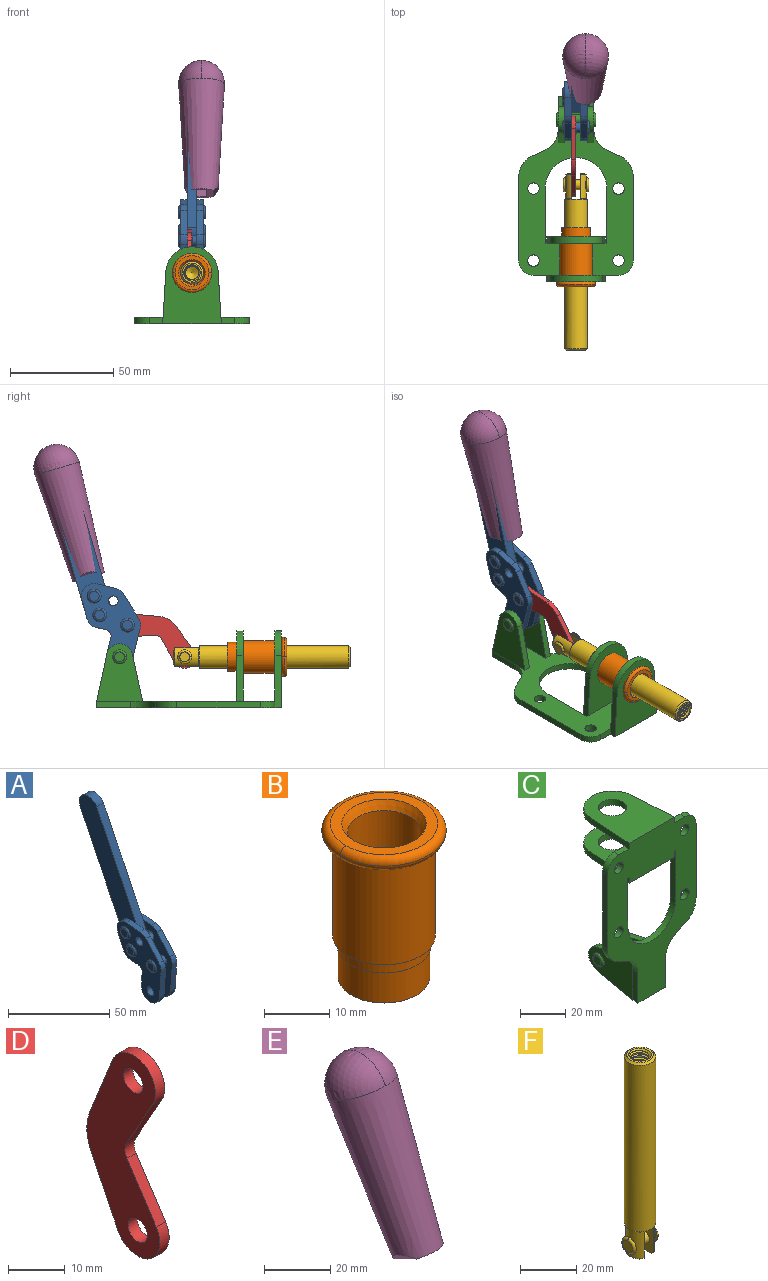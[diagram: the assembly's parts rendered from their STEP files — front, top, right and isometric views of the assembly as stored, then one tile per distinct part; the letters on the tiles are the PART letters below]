
ASSEMBLY  parts=6 mates=6
PART A: 59 faces, bbox 12.9x60.2x99.6 mm
  f0: torus R=2.39mm, axis (-1,0,0), area 14.9mm2, adj f20,f43,f51
  f1: torus R=2.39mm, axis (-1,0,0), area 14.9mm2, adj f19,f42,f51
  f2: torus R=2.39mm, axis (-1,0,0), area 14.9mm2, adj f18,f35,f51
  f3: torus R=2.39mm, axis (-1,0,0), area 14.9mm2, adj f14,f17,f23
  f4: torus R=2.39mm, axis (-1,0,0), area 14.9mm2, adj f13,f16,f23
  f5: torus R=2.39mm, axis (-1,0,0), area 14.9mm2, adj f12,f15,f23
  f6: cylinder r=2.39mm len=4.78mm, axis (1,0,0), area 46.5mm2, adj f48,f50,f51
  f7: cylinder r=2.39mm len=4.78mm, axis (1,0,0), area 46.5mm2, adj f50,f51
  f8: cylinder r=6.35mm len=12.68mm, axis (1,0,0), area 61.8mm2, adj f38,f39,f50,f51
  f9: cylinder r=2.39mm len=4.78mm, axis (-1,0,0), area 70.5mm2, adj f46,f50
  f10: cylinder r=2.39mm len=4.78mm, axis (-1,0,0), area 46.5mm2, adj f23,f45,f46
  f11: cylinder r=2.39mm len=4.78mm, axis (-1,0,0), area 46.5mm2, adj f23,f46
  f12: plane 4.78x4.78mm, normal (1,0,0), area 17.9mm2, adj f5,f15
  f13: plane 4.78x4.78mm, normal (1,0,0), area 17.9mm2, adj f4,f16
  f14: plane 4.78x4.78mm, normal (1,0,0), area 17.9mm2, adj f3,f17
  f15: torus R=2.39mm, axis (-1,0,0), area 14.9mm2, adj f5,f12,f23
  f16: torus R=2.39mm, axis (-1,0,0), area 14.9mm2, adj f4,f13,f23
  f17: torus R=2.39mm, axis (-1,0,0), area 14.9mm2, adj f3,f14,f23
  f18: plane 4.78x4.78mm, normal (-1,0,0), area 17.9mm2, adj f2,f35
  f19: plane 4.78x4.78mm, normal (-1,0,0), area 17.9mm2, adj f1,f42
  f20: plane 4.78x4.78mm, normal (-1,0,0), area 17.9mm2, adj f0,f43
  f21: plane 2.26x0.2mm, normal (1,0,0), area 0.2mm2, adj f31,f44
  f22: plane 2.26x0.2mm, normal (-1,0,0), area 0.2mm2, adj f41,f44
  f23: plane 39.37x30.77mm, normal (1,0,0), area 565.5mm2, adj f3,f4,f5,f10,f11,f15,f16,f17
  f24: cylinder r=6.1mm len=4.15mm, axis (-1,0,0), area 14.7mm2, adj f23,f25,f32,f46
  f25: plane 10.25x9.01mm, normal (0,-0.75,0.66), area 42.3mm2, adj f23,f24,f26,f46
  f26: cylinder r=6.35mm len=4.64mm, axis (-1,0,0), area 15.6mm2, adj f23,f25,f27,f46
  f27: plane 15.84x3.1mm, normal (0,-1,-0.07), area 49.2mm2, adj f23,f26,f28,f46
  f28: cylinder r=6.35mm len=12.68mm, axis (-1,0,0), area 61.8mm2, adj f23,f27,f29,f46
  f29: plane 8.11x3.1mm, normal (0,1,0.07), area 25.2mm2, adj f23,f28,f30,f46
  f30: cylinder r=3.05mm len=3.25mm, axis (-1,0,0), area 14.8mm2, adj f23,f29,f31,f46
  f31: plane 5.99x3.1mm, normal (0,0.07,-1), area 18.6mm2, adj f21,f23,f30,f44,f46
  f32: plane 9.5x3.1mm, normal (0,-0.07,1), area 29.5mm2, adj f23,f24,f33,f46,f47
  f33: cylinder r=6.1mm len=8.63mm, axis (-1,0,0), area 39.1mm2, adj f23,f32,f34,f47
  f34: plane 8.65x3.96mm, normal (0,0.91,-0.42), area 29.5mm2, adj f23,f33,f44,f47
  f35: torus R=2.39mm, axis (-1,0,0), area 14.9mm2, adj f2,f18,f51
  f36: plane 10.25x9.01mm, normal (0,-0.75,0.66), area 42.3mm2, adj f37,f49,f50,f51
  f37: cylinder r=6.35mm len=4.64mm, axis (1,0,0), area 15.6mm2, adj f36,f38,f50,f51
  f38: plane 15.84x3.1mm, normal (0,-1,-0.07), area 49.2mm2, adj f8,f37,f50,f51
  f39: plane 8.11x3.1mm, normal (0,1,0.07), area 25.2mm2, adj f8,f40,f50,f51
  f40: cylinder r=3.05mm len=3.25mm, axis (1,0,0), area 14.8mm2, adj f39,f41,f50,f51
  f41: plane 5.99x3.1mm, normal (0,0.07,-1), area 18.6mm2, adj f22,f40,f44,f50,f51
  f42: torus R=2.39mm, axis (-1,0,0), area 14.9mm2, adj f1,f19,f51
  f43: torus R=2.39mm, axis (-1,0,0), area 14.9mm2, adj f0,f20,f51
  f44: cylinder r=6.35mm len=12.12mm, axis (-1,0,0), area 128.9mm2, adj f21,f22,f23,f31,f34,f41,f46,f47
  f45: plane 2.65x1.35mm, normal (1,0,0), area 1mm2, adj f10,f55
  f46: plane 39.08x20.42mm, normal (-1,0,0), area 412.5mm2, adj f9,f10,f11,f24,f25,f26,f27,f28
  f47: plane 77.62x39.82mm, normal (1,0,0), area 850mm2, adj f32,f33,f34,f44,f53,f54,f55
  f48: plane 2.65x1.35mm, normal (-1,0,0), area 1mm2, adj f6,f55
  f49: cylinder r=6.1mm len=4.15mm, axis (1,0,0), area 14.7mm2, adj f36,f50,f51,f56
  f50: plane 39.08x20.42mm, normal (1,0,0), area 412.5mm2, adj f6,f7,f8,f9,f36,f37,f38,f39
  f51: plane 39.37x30.77mm, normal (-1,0,0), area 565.5mm2, adj f0,f1,f2,f6,f7,f8,f35,f36
  f52: plane 8.65x3.96mm, normal (0,0.91,-0.42), area 29.5mm2, adj f44,f51,f57,f58
  f53: plane 68.49x33.4mm, normal (0,0.9,-0.44), area 358.1mm2, adj f44,f47,f54,f58
  f54: cylinder r=6.35mm len=12.06mm, axis (1,0,0), area 93.7mm2, adj f47,f53,f55,f58
  f55: plane 68.49x33.4mm, normal (0,-0.9,0.44), area 358.1mm2, adj f44,f45,f46,f47,f48,f50,f54,f58
  f56: plane 9.5x3.1mm, normal (0,-0.07,1), area 29.5mm2, adj f49,f50,f51,f57,f58
  f57: cylinder r=6.1mm len=8.63mm, axis (1,0,0), area 39.1mm2, adj f51,f52,f56,f58
  f58: plane 77.62x39.82mm, normal (-1,0,0), area 850mm2, adj f44,f52,f53,f54,f55,f56,f57
PART B: 15 faces, bbox 20.6x20.6x28.7 mm
  f0: torus R=8.26mm, axis (0,0,1), area 56.8mm2, adj f1,f10,f12
  f1: torus R=8.26mm, axis (0,0,1), area 56.8mm2, adj f0,f6,f13
  f2: cylinder r=5.59mm len=25.91mm, axis (0,0,1), area 909.6mm2, adj f3,f4
  f3: cone r=6.86mm half-angle=45deg, axis (0,0,-1), area 70.2mm2, adj f2,f14
  f4: cone r=6.47mm half-angle=30deg, axis (0,0,1), area 66.7mm2, adj f2,f13
  f5: cylinder r=7.04mm len=14.07mm, axis (0,0,1), area 252.6mm2, adj f11,f14
  f6: torus R=8.26mm, axis (0,0,1), area 56.8mm2, adj f1,f12,f13
  f7: cylinder r=7.16mm len=14.33mm, axis (0,0,1), area 91.5mm2, adj f9,f11
  f8: cylinder r=7.86mm len=18.42mm, axis (0,0,1), area 909.6mm2, adj f9,f10
  f9: plane 15.72x15.72mm, normal (0,0,-1), area 33mm2, adj f7,f8
  f10: plane 16.51x16.51mm, normal (0,0,-1), area 19.9mm2, adj f0,f8,f12
  f11: plane 14.33x14.33mm, normal (0,0,-1), area 5.7mm2, adj f5,f7
  f12: torus R=8.26mm, axis (0,0,1), area 56.8mm2, adj f0,f6,f10
  f13: plane 16.51x16.51mm, normal (0,0,1), area 82.7mm2, adj f1,f4,f6
  f14: plane 14.07x14.07mm, normal (0,0,-1), area 7.8mm2, adj f3,f5
PART C: 55 faces, bbox 55.7x37.4x89.8 mm
  f0: torus R=2.41mm, axis (-1,0,0), area 15mm2, adj f11,f15,f25
  f1: torus R=2.41mm, axis (-1,0,0), area 15mm2, adj f10,f12,f22
  f2: cylinder r=2.78mm len=5.56mm, axis (0,-1,0), area 54.2mm2, adj f30,f54
  f3: cylinder r=14.99mm len=29.97mm, axis (0,-1,0), area 145.9mm2, adj f30,f49,f53,f54
  f4: cylinder r=2.78mm len=5.56mm, axis (0,-1,0), area 54.2mm2, adj f30,f54
  f5: cylinder r=2.78mm len=5.56mm, axis (0,-1,0), area 54.2mm2, adj f30,f54
  f6: cylinder r=2.78mm len=5.56mm, axis (0,-1,0), area 54.2mm2, adj f30,f54
  f7: cylinder r=6.35mm len=12.7mm, axis (0,0,1), area 123.6mm2, adj f27,f51
  f8: cylinder r=6.35mm len=12.7mm, axis (0,0,-1), area 124.7mm2, adj f21,f35
  f9: cylinder r=2.41mm len=11.18mm, axis (-1,0,0), area 169.4mm2, adj f16,f19
  f10: plane 4.83x4.83mm, normal (1,0,0), area 18.3mm2, adj f1,f12
  f11: plane 4.83x4.83mm, normal (-1,0,0), area 18.3mm2, adj f0,f15
  f12: torus R=2.41mm, axis (-1,0,0), area 15mm2, adj f1,f10,f22
  f13: cylinder r=6.35mm len=12.41mm, axis (1,0,0), area 53.4mm2, adj f18,f19,f22,f23
  f14: cylinder r=6.35mm len=12.41mm, axis (-1,0,0), area 53.4mm2, adj f16,f17,f24,f25
  f15: torus R=2.41mm, axis (-1,0,0), area 15mm2, adj f0,f11,f25
  f16: plane 27.86x22.35mm, normal (1,0,0), area 425.4mm2, adj f9,f14,f17,f24,f30
  f17: plane 22.86x4.97mm, normal (0,0.21,0.98), area 72.5mm2, adj f14,f16,f25,f30
  f18: plane 22.86x4.97mm, normal (0,0.21,0.98), area 72.5mm2, adj f13,f19,f22,f30
  f19: plane 27.86x22.35mm, normal (-1,0,0), area 425.4mm2, adj f9,f13,f18,f23,f30
  f20: cylinder r=12.7mm len=25.35mm, axis (0,0,-1), area 119.8mm2, adj f21,f34,f35,f36
  f21: plane 34.21x28.07mm, normal (0,0,-1), area 702.4mm2, adj f8,f20,f30,f34,f36
  f22: plane 27.96x22.45mm, normal (1,0,0), area 407.2mm2, adj f1,f12,f13,f18,f23,f30,f42,f43
  f23: plane 22.86x4.97mm, normal (0,0.21,-0.98), area 72.5mm2, adj f13,f19,f22,f44
  f24: plane 22.86x4.97mm, normal (0,0.21,-0.98), area 72.5mm2, adj f14,f16,f25,f44
  f25: plane 27.86x22.35mm, normal (-1,0,0), area 407.1mm2, adj f0,f14,f15,f17,f24,f30,f45,f46
  f26: plane 3.1x0.95mm, normal (0,0,-1), area 2.7mm2, adj f30,f49,f50,f54
  f27: plane 34.21x28.07mm, normal (0,0,1), area 702.4mm2, adj f7,f28,f30,f50,f52
  f28: cylinder r=12.7mm len=25.35mm, axis (0,0,1), area 118.8mm2, adj f27,f50,f51,f52
  f29: plane 3.1x0.95mm, normal (0,0,-1), area 2.7mm2, adj f30,f52,f53,f54
  f30: plane 86.54x55.63mm, normal (0,1,0), area 2362.9mm2, adj f2,f3,f4,f5,f6,f16,f17,f18
  f31: plane 40.56x3.1mm, normal (-1,0,0), area 125.7mm2, adj f30,f32,f48,f54
  f32: cylinder r=7.11mm len=7.11mm, axis (0,-1,0), area 34.6mm2, adj f30,f31,f33,f54
  f33: plane 6.67x3.1mm, normal (0,0,1), area 20.4mm2, adj f30,f32,f34,f54
  f34: plane 25.39x3.13mm, normal (-1,0.06,0), area 79.5mm2, adj f20,f21,f33,f35,f54
  f35: plane 37.31x28.45mm, normal (0,0,1), area 789.9mm2, adj f8,f20,f34,f36,f54
  f36: plane 25.39x3.13mm, normal (1,0.06,0), area 79.5mm2, adj f20,f21,f35,f37,f54
  f37: plane 6.67x3.1mm, normal (0,0,1), area 20.4mm2, adj f30,f36,f38,f54
  f38: cylinder r=7.11mm len=7.11mm, axis (0,-1,0), area 34.6mm2, adj f30,f37,f39,f54
  f39: plane 40.56x3.1mm, normal (1,0,0), area 125.7mm2, adj f30,f38,f40,f54
  f40: cylinder r=11.18mm len=10.16mm, axis (0,-1,0), area 39.5mm2, adj f30,f39,f41,f54
  f41: plane 6.09x3.1mm, normal (0.42,0,-0.91), area 20.8mm2, adj f30,f40,f42,f54
  f42: cylinder r=11.18mm len=9.41mm, axis (0,-1,0), area 37.2mm2, adj f22,f30,f41,f43,f54
  f43: plane 16.5x3.1mm, normal (1,0,0), area 51.1mm2, adj f22,f42,f44,f54
  f44: plane 17.37x3.1mm, normal (0,0,-1), area 53.8mm2, adj f23,f24,f30,f43,f45,f54
  f45: plane 16.5x3.1mm, normal (-1,0,0), area 51.1mm2, adj f25,f44,f46,f54
  f46: cylinder r=11.18mm len=9.41mm, axis (0,-1,0), area 37.2mm2, adj f25,f30,f45,f47,f54
  f47: plane 6.09x3.1mm, normal (-0.42,0,-0.91), area 20.8mm2, adj f30,f46,f48,f54
  f48: cylinder r=11.18mm len=10.16mm, axis (0,-1,0), area 39.5mm2, adj f30,f31,f47,f54
  f49: plane 26.54x3.1mm, normal (-1,0,0), area 82.3mm2, adj f3,f26,f30,f54
  f50: plane 25.39x3.1mm, normal (1,0.06,0), area 78.8mm2, adj f26,f27,f28,f51,f54
  f51: plane 37.31x28.45mm, normal (0,0,-1), area 789.9mm2, adj f7,f28,f50,f52,f54
  f52: plane 25.39x3.1mm, normal (-1,0.06,0), area 78.8mm2, adj f27,f28,f29,f51,f54
  f53: plane 26.54x3.1mm, normal (1,0,0), area 82.3mm2, adj f3,f29,f30,f54
  f54: plane 89.66x55.63mm, normal (0,-1,0), area 2678.5mm2, adj f2,f3,f4,f5,f6,f26,f29,f31
PART D: 12 faces, bbox 2.3x18.2x42.8 mm
  f0: cylinder r=2.4mm len=4.8mm, axis (1,0,0), area 34.9mm2, adj f4,f11
  f1: cylinder r=10.41mm len=8.47mm, axis (1,0,0), area 20.2mm2, adj f4,f9,f10,f11
  f2: cylinder r=3.05mm len=3.16mm, axis (1,0,0), area 7.7mm2, adj f4,f6,f7,f11
  f3: cylinder r=2.4mm len=4.8mm, axis (1,0,0), area 34.9mm2, adj f4,f11
  f4: plane 42.81x18.23mm, normal (-1,0,0), area 414.1mm2, adj f0,f1,f2,f3,f5,f6,f7,f8
  f5: cylinder r=5.54mm len=10.67mm, axis (1,0,0), area 41.8mm2, adj f4,f6,f10,f11
  f6: plane 11.66x6.53mm, normal (0,-0.87,-0.49), area 30.9mm2, adj f2,f4,f5,f11
  f7: plane 11.17x7.33mm, normal (0,-0.84,0.55), area 30.9mm2, adj f2,f4,f8,f11
  f8: cylinder r=5.54mm len=10.51mm, axis (1,0,0), area 41.8mm2, adj f4,f7,f9,f11
  f9: plane 13.67x6.67mm, normal (0,0.9,-0.44), area 35.1mm2, adj f1,f4,f8,f11
  f10: plane 14.1x5.7mm, normal (0,0.93,0.37), area 35.1mm2, adj f1,f4,f5,f11
  f11: plane 42.81x18.23mm, normal (1,0,0), area 414.1mm2, adj f0,f1,f2,f3,f5,f6,f7,f8
PART E: 11 faces, bbox 22.3x42.6x64.5 mm
  f0: sphere r=11.13mm, area 411.4mm2, adj f1,f8
  f1: cone r=11.11mm half-angle=3.3deg, axis (0,0.44,0.9), area 3251.8mm2, adj f0,f7,f8,f9,f10
  f2: cylinder r=6.16mm len=11.7mm, axis (1,0,0), area 89.5mm2, adj f3,f4,f5,f6
  f3: plane 60.23x36.75mm, normal (-1,0,0), area 763.6mm2, adj f2,f4,f6,f10
  f4: plane 51.37x25.05mm, normal (0,0.9,-0.44), area 264.2mm2, adj f2,f3,f5,f10
  f5: plane 60.23x36.75mm, normal (1,0,0), area 763.6mm2, adj f2,f4,f6,f10
  f6: plane 51.37x25.05mm, normal (0,-0.9,0.44), area 264.2mm2, adj f2,f3,f5,f10
  f7: plane 9.95x5.95mm, normal (0.71,-0.31,-0.64), area 25.8mm2, adj f1,f10
  f8: sphere r=11.13mm, area 411.4mm2, adj f0,f1
  f9: plane 9.95x5.95mm, normal (-0.71,-0.31,-0.64), area 25.8mm2, adj f1,f10
  f10: plane 14.27x11.38mm, normal (0,-0.44,-0.9), area 106.7mm2, adj f1,f3,f4,f5,f6,f7,f9
PART F: 48 faces, bbox 12.6x11.1x86.1 mm
  f0: torus R=2.41mm, axis (-1,0,0), area 15mm2, adj f30,f32,f34
  f1: torus R=2.41mm, axis (-1,0,0), area 15mm2, adj f29,f31,f33
  f2: cylinder r=5.54mm len=72.39mm, axis (0,0,1), area 2518.5mm2, adj f3,f4,f42,f43
  f3: cone r=5.54mm half-angle=45deg, axis (0,0,1), area 7.6mm2, adj f2,f5,f41
  f4: cone r=5.54mm half-angle=45deg, axis (0,0,-1), area 34.9mm2, adj f2,f39
  f5: cylinder r=5.08mm len=11.48mm, axis (0,0,1), area 108.3mm2, adj f3,f7,f8,f41
  f6: cylinder r=2.41mm len=4.83mm, axis (-1,0,0), area 71.2mm2, adj f40,f41
  f7: cylinder r=2.41mm len=4.83mm, axis (-1,0,0), area 7.6mm2, adj f5,f34
  f8: cone r=5.08mm half-angle=45deg, axis (0,0,1), area 10.6mm2, adj f5,f37,f41
  f9: cone r=3.98mm half-angle=45deg, axis (0,0,1), area 17.6mm2, adj f27,f39,f45,f46,f47
  f10: cylinder r=2.41mm len=4.83mm, axis (-1,0,0), area 7.6mm2, adj f33,f38
  f11: cylinder r=3.2mm len=6.4mm, axis (0,0,1), area 78.4mm2, adj f12,f28,f44,f45,f47
  f12: cylinder r=3.2mm len=6.4mm, axis (0,0,1), area 10.5mm2, adj f11,f13,f45,f47
  f13: cylinder r=3.2mm len=6.4mm, axis (0,0,1), area 10.5mm2, adj f12,f14,f45,f47
  f14: cylinder r=3.2mm len=6.4mm, axis (0,0,1), area 10.5mm2, adj f13,f15,f45,f47
  f15: cylinder r=3.2mm len=6.4mm, axis (0,0,1), area 10.5mm2, adj f14,f16,f45,f47
  f16: cylinder r=3.2mm len=6.4mm, axis (0,0,1), area 10.5mm2, adj f15,f17,f45,f47
  f17: cylinder r=3.2mm len=6.4mm, axis (0,0,1), area 10.5mm2, adj f16,f18,f45,f47
  f18: cylinder r=3.2mm len=6.4mm, axis (0,0,1), area 10.5mm2, adj f17,f19,f45,f47
  f19: cylinder r=3.2mm len=6.4mm, axis (0,0,1), area 10.5mm2, adj f18,f20,f45,f47
  f20: cylinder r=3.2mm len=6.4mm, axis (0,0,1), area 10.5mm2, adj f19,f21,f45,f47
  f21: cylinder r=3.2mm len=6.4mm, axis (0,0,1), area 10.5mm2, adj f20,f22,f45,f47
  f22: cylinder r=3.2mm len=6.4mm, axis (0,0,1), area 10.5mm2, adj f21,f23,f45,f47
  f23: cylinder r=3.2mm len=6.4mm, axis (0,0,1), area 10.5mm2, adj f22,f24,f45,f47
  f24: cylinder r=3.2mm len=6.4mm, axis (0,0,1), area 10.5mm2, adj f23,f25,f45,f47
  f25: cylinder r=3.2mm len=6.4mm, axis (0,0,1), area 10.5mm2, adj f24,f26,f45,f47
  f26: cylinder r=3.2mm len=6.4mm, axis (0,0,1), area 10.5mm2, adj f25,f27,f45,f47
  f27: cylinder r=3.2mm len=6.4mm, axis (0,0,1), area 7.4mm2, adj f9,f26,f45,f47
  f28: cone r=3.2mm half-angle=60deg, axis (0,0,1), area 37.2mm2, adj f11
  f29: plane 4.83x4.83mm, normal (-1,0,0), area 18.3mm2, adj f1,f31
  f30: plane 4.83x4.83mm, normal (1,0,0), area 18.3mm2, adj f0,f32
  f31: torus R=2.41mm, axis (-1,0,0), area 15mm2, adj f1,f29,f33
  f32: torus R=2.41mm, axis (-1,0,0), area 15mm2, adj f0,f30,f34
  f33: plane 6.83x6.83mm, normal (1,0,0), area 18.3mm2, adj f1,f10,f31
  f34: plane 6.83x6.83mm, normal (-1,0,0), area 18.3mm2, adj f0,f7,f32
  f35: cone r=5.08mm half-angle=45deg, axis (0,0,1), area 10.6mm2, adj f36,f38,f40
  f36: plane 7.25x1.97mm, normal (0,0,-1), area 10mm2, adj f35,f40
  f37: plane 7.25x1.97mm, normal (0,0,-1), area 10mm2, adj f8,f41
  f38: cylinder r=5.08mm len=11.48mm, axis (0,0,1), area 108.3mm2, adj f10,f35,f40,f42
  f39: plane 9.55x9.55mm, normal (0,0,1), area 22mm2, adj f4,f9
  f40: plane 12.76x10.09mm, normal (1,0,0), area 95.7mm2, adj f6,f35,f36,f38,f42,f43
  f41: plane 12.76x10.09mm, normal (-1,0,0), area 95.7mm2, adj f3,f5,f6,f8,f37,f43
  f42: cone r=5.54mm half-angle=45deg, axis (0,0,1), area 7.6mm2, adj f2,f38,f40
  f43: plane 11.07x4.7mm, normal (0,0,-1), area 50.4mm2, adj f2,f40,f41
  f44: plane 0.89x0.62mm, normal (-1,0,0), area 0.3mm2, adj f11,f45,f46,f47
  f45: bspline ~24.8x7.63mm, area 266.6mm2, adj f9,f11,f12,f13,f14,f15,f16,f17
  f46: bspline ~24.87x7.63mm, area 73.6mm2, adj f9,f44,f45,f47
  f47: bspline ~24.98x7.63mm, area 272.5mm2, adj f9,f11,f12,f13,f14,f15,f16,f17
PLACE A rot(axis=(1,0,0),9.8deg) t=(0,11.8,52.04)mm
PLACE B rot(axis=(1,0,0),90deg) t=(0,9.43,0)mm
PLACE C rot(axis=(1,0,0),90deg) t=(0,9.43,0)mm fixed
PLACE D rot(axis=(1,0,0),121deg) t=(-1.16,35.92,11.51)mm
PLACE E rot(axis=(1,0,0),9.8deg) t=(4.66,11.8,52.04)mm
PLACE F rot(axis=(1,0,0),90deg) t=(0,25.45,0)mm
MATE slider F.f2 <-> C.f7  axis (0,-1,0) through (0,-33.33,24.61)mm
MATE fastened B.f2 <-> C.f7  axis (0,-1,0) through (0,-36.96,24.61)mm
MATE revolute A.f4 <-> D.f3  axis (-1,0,0) through (0,37.73,40.03)mm
MATE revolute A.f7 <-> C.f0  axis (-1,0,0) through (0,41.52,24.61)mm
MATE fastened E.f2 <-> A.f54  axis (1,0,0) through (2.35,72.46,118.12)mm
MATE revolute F.f6 <-> D.f5  axis (-1,0,0) through (0,9.97,24.61)mm
